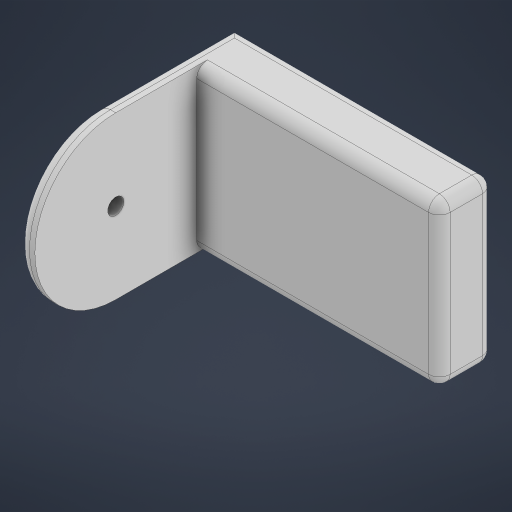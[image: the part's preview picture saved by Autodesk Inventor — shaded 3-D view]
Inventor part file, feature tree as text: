
AUTODESK INVENTOR PART (.ipt)
format: ipt  version: 2023 (Build 270158000, 158)  size: 206,848 bytes
history: native  units: mm
features: extrude x3, sketch x3, fillet x2
ambient origin geometry x8: Origin, YZ Plane, XZ Plane, XY Plane, X Axis, Y Axis, Z Axis, Center Point
bodies: Solid1 (feature_tree)
feature tree (8):
  extrude  "Extrusion1"  Depth=30.0mm
  extrude  "Extrusion2"  Depth=3.0mm
  fillet  "Fillet1"  Radius=15.0mm
  extrude  "Extrusion3"  Depth=3.0mm
  fillet  "Fillet2"  Radius=30.0mm
  sketch  "Sketch1"  dims[d0=45.0mm d1=30.0mm]
  sketch  "Sketch2"  dims[d2=10.0mm d3=0.0mm d4=3.0mm]
  sketch  "Sketch3"  dims[d5=30.0mm d6=10.0mm d7=0.0mm d8=0.0mm d9=15.0mm d10=3.0mm d11=30.0mm d12=0.0mm d13=2.0mm]
